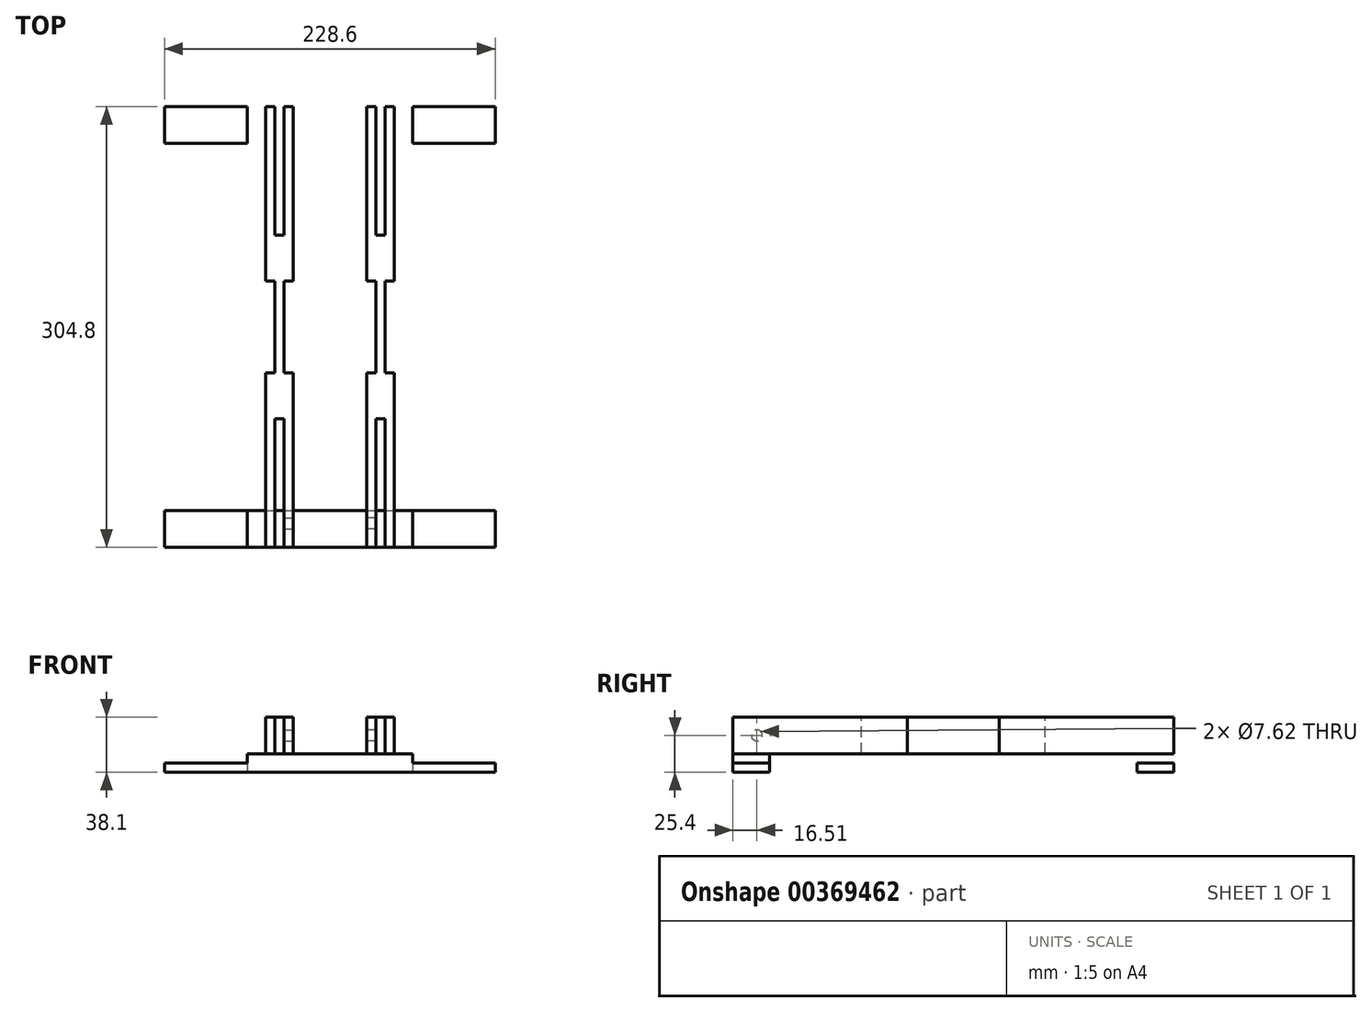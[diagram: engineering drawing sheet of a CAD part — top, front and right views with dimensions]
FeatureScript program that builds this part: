
annotation { "Feature Type Name" : "Feature", "Feature Type Description" : "" }
export const myFeature = defineFeature(function(context is Context, id is Id, definition is map)
    precondition{}
    {
        {
            var Q0;
            Q0=qCreatedBy(makeId("Top.planeOp"),FACE);
            var sketch = newSketch(context, id + "F0", { "sketchPlane" : qUnion([Q0])});
            skLineSegment(sketch, "E0.bottom", {"start": v(-114.3, 152.4) * mm, "end": v(114.3, 152.4) * mm});
            skLineSegment(sketch, "E0.top", {"start": v(-114.3, 127) * mm, "end": v(114.3, 127) * mm});
            skLineSegment(sketch, "E0.left", {"start": v(-114.3, 152.4) * mm, "end": v(-114.3, 127) * mm});
            skLineSegment(sketch, "E0.right", {"start": v(114.3, 152.4) * mm, "end": v(114.3, 127) * mm});
            skLineSegment(sketch, "E1", {"start": v(-113.97, 0) * mm, "end": v(125.77, 0) * mm});
            skLineSegment(sketch, "E2.MirrorCS", {"start": v(-114.3, -152.4) * mm, "end": v(114.3, -152.4) * mm});
            skLineSegment(sketch, "E3.MirrorCS", {"start": v(-114.3, -152.4) * mm, "end": v(-114.3, -127) * mm});
            skLineSegment(sketch, "E4.MirrorCS", {"start": v(-114.3, -127) * mm, "end": v(114.3, -127) * mm});
            skLineSegment(sketch, "E5.MirrorCS", {"start": v(114.3, -152.4) * mm, "end": v(114.3, -127) * mm});
            skLineSegment(sketch, "E6.bottom", {"start": v(-57.15, 152.4) * mm, "end": v(57.15, 152.4) * mm});
            skLineSegment(sketch, "E6.top", {"start": v(-57.15, 127) * mm, "end": v(57.15, 127) * mm});
            skLineSegment(sketch, "E6.left", {"start": v(-57.15, 152.4) * mm, "end": v(-57.15, 127) * mm});
            skLineSegment(sketch, "E6.right", {"start": v(57.15, 152.4) * mm, "end": v(57.15, 127) * mm});
            skLineSegment(sketch, "E7.MirrorCS", {"start": v(-57.15, -127) * mm, "end": v(57.15, -127) * mm});
            skLineSegment(sketch, "E8.MirrorCS", {"start": v(-57.15, -152.4) * mm, "end": v(-57.15, -127) * mm});
            skLineSegment(sketch, "E9.MirrorCS", {"start": v(57.15, -152.4) * mm, "end": v(57.15, -127) * mm});
            skLineSegment(sketch, "E10.MirrorCS", {"start": v(-57.15, -152.4) * mm, "end": v(57.15, -152.4) * mm});
            skLineSegment(sketch, "E11", {"start": v(0, 0) * mm, "end": v(0, -127) * mm});
            skSolve(sketch);
        }
        {
            var Q0;
            {var subQ0=sQuery(id+"F0.wireOp",EDGE,"E5.MirrorCS");Q0=makeQuery(id+"F0.imprint","IMPRINT",FACE,{"disambiguationData":[TD([[makeQuery(id+"F0.imprint","IMPRINT",EDGE,{"derivedFrom":subQ0}),1.0]])]});}
            var Q1;
            {var subQ0=sQuery(id+"F0.wireOp",EDGE,"E3.MirrorCS");Q1=makeQuery(id+"F0.imprint","IMPRINT",FACE,{"disambiguationData":[TD([[makeQuery(id+"F0.imprint","IMPRINT",EDGE,{"derivedFrom":subQ0}),-1.0]])]});}
            var Q2;
            {var subQ0=sQuery(id+"F0.wireOp",EDGE,"E0.left");Q2=makeQuery(id+"F0.imprint","IMPRINT",FACE,{"disambiguationData":[TD([[makeQuery(id+"F0.imprint","IMPRINT",EDGE,{"derivedFrom":subQ0}),1.0]])]});}
            var Q3;
            {var subQ0=sQuery(id+"F0.wireOp",EDGE,"E0.right");Q3=makeQuery(id+"F0.imprint","IMPRINT",FACE,{"disambiguationData":[TD([[makeQuery(id+"F0.imprint","IMPRINT",EDGE,{"derivedFrom":subQ0}),-1.0]])]});}
            extrude(context, id + "F1", {"entities" : qUnion([Q0, Q1, Q2, Q3]), "depth" : 6.35 * mm});
        }
        {
            var Q0;
            Q0=makeQuery(id+"F0.imprint","IMPRINT",FACE,{"disambiguationData":[TD([[makeQuery(id+"F0.imprint","IMPRINT",EDGE,{"derivedFrom":sQuery(id+"F0.wireOp",EDGE,"E8.MirrorCS")}),-1.0]])]});
            var Q1;
            Q1=makeQuery(id+"F0.imprint","IMPRINT",FACE,{"disambiguationData":[TD([[makeQuery(id+"F0.imprint","IMPRINT",EDGE,{"derivedFrom":sQuery(id+"F0.wireOp",EDGE,"E6.bottom")}),-1.0]])]});
            extrude(context, id + "F2", {"entities" : qUnion([Q0, Q1]), "depth" : 12.7 * mm});
        }
        {
            var Q0;
            Q0=makeQuery(id+"F1.opExtrude","SWEPT_BODY",BODY,{"disambiguationData":[OSD([sQuery(id+"F0.wireOp",EDGE,"E0.bottom"),sQuery(id+"F0.wireOp",EDGE,"E0.top"),sQuery(id+"F0.wireOp",EDGE,"E0.left"),sQuery(id+"F0.wireOp",EDGE,"E6.left")])]});
            var Q1;
            Q1=makeQuery(id+"F1.opExtrude","SWEPT_BODY",BODY,{"disambiguationData":[OSD([sQuery(id+"F0.wireOp",EDGE,"E0.bottom"),sQuery(id+"F0.wireOp",EDGE,"E0.top"),sQuery(id+"F0.wireOp",EDGE,"E0.right"),sQuery(id+"F0.wireOp",EDGE,"E6.right")])]});
            var Q2;
            Q2=makeQuery(id+"F1.opExtrude","SWEPT_BODY",BODY,{"disambiguationData":[OSD([sQuery(id+"F0.wireOp",EDGE,"E2.MirrorCS"),sQuery(id+"F0.wireOp",EDGE,"E3.MirrorCS"),sQuery(id+"F0.wireOp",EDGE,"E4.MirrorCS"),sQuery(id+"F0.wireOp",EDGE,"E8.MirrorCS")])]});
            var Q3;
            Q3=makeQuery(id+"F1.opExtrude","SWEPT_BODY",BODY,{"disambiguationData":[OSD([sQuery(id+"F0.wireOp",EDGE,"E2.MirrorCS"),sQuery(id+"F0.wireOp",EDGE,"E4.MirrorCS"),sQuery(id+"F0.wireOp",EDGE,"E5.MirrorCS"),sQuery(id+"F0.wireOp",EDGE,"E9.MirrorCS")])]});
            var Q4;
            Q4=makeQuery(id+"F2.opExtrude","SWEPT_BODY",BODY,{"disambiguationData":[OSD([sQuery(id+"F0.wireOp",EDGE,"E6.bottom"),sQuery(id+"F0.wireOp",EDGE,"E6.top"),sQuery(id+"F0.wireOp",EDGE,"E6.left"),sQuery(id+"F0.wireOp",EDGE,"E6.right")])]});
            var Q5;
            Q5=makeQuery(id+"F2.opExtrude","SWEPT_BODY",BODY,{"disambiguationData":[OSD([sQuery(id+"F0.wireOp",EDGE,"E8.MirrorCS"),sQuery(id+"F0.wireOp",EDGE,"E9.MirrorCS"),sQuery(id+"F0.wireOp",EDGE,"E10.MirrorCS"),sQuery(id+"F0.wireOp",EDGE,"E7.MirrorCS")])]});
            booleanBodies(context, id + "F3", {"operationType" : BooleanOperationType.UNION, "tools" : qUnion([Q0, Q1, Q2, Q3, Q4, Q5])});
        }
        {
            var Q0;
            {var subQ0=sQuery(id+"F0.wireOp",EDGE,"E10.MirrorCS");var subQ1=sQuery(id+"F0.wireOp",EDGE,"E2.MirrorCS");Q0=makeQuery(id+"F3.opBoolean","MERGE",FACE,{"derivedFrom":[makeQuery(id+"F1.opExtrude","SWEPT_FACE",FACE,{"disambiguationData":[OSD([subQ1]),TDD([makeQuery(id+"F0.imprint","IMPRINT",EDGE,{"disambiguationData":[TD([[makeQuery(id+"F0.imprint","INTERSECT",VERTEX,{"derivedFrom":[subQ1,sQuery(id+"F0.wireOp",EDGE,"E3.MirrorCS")]}),-1.0]])],"derivedFrom":subQ1})])]}),makeQuery(id+"F1.opExtrude","SWEPT_FACE",FACE,{"disambiguationData":[OSD([subQ1]),TDD([makeQuery(id+"F0.imprint","IMPRINT",EDGE,{"disambiguationData":[TD([[makeQuery(id+"F0.imprint","INTERSECT",VERTEX,{"derivedFrom":[subQ1,sQuery(id+"F0.wireOp",EDGE,"E5.MirrorCS")]}),1.0]])],"derivedFrom":subQ1})])]}),makeQuery(id+"F2.opExtrude","SWEPT_FACE",FACE,{"disambiguationData":[OSD([subQ0])]})]});}
            var sketch = newSketch(context, id + "F4", { "sketchPlane" : qUnion([Q0])});
            skLineSegment(sketch, "E12", {"start": v(0, 59.29) * mm, "end": v(0, 0) * mm});
            skLineSegment(sketch, "E13.bottom", {"start": v(-44.45, 12.7) * mm, "end": v(-38.1, 12.7) * mm});
            skLineSegment(sketch, "E13.top", {"start": v(-44.45, 38.1) * mm, "end": v(-38.1, 38.1) * mm});
            skLineSegment(sketch, "E13.left", {"start": v(-44.45, 12.7) * mm, "end": v(-44.45, 38.1) * mm});
            skLineSegment(sketch, "E13.right", {"start": v(-38.1, 12.7) * mm, "end": v(-38.1, 38.1) * mm});
            skLineSegment(sketch, "E14.bottom", {"start": v(-31.75, 12.7) * mm, "end": v(-25.4, 12.7) * mm});
            skLineSegment(sketch, "E14.top", {"start": v(-31.75, 38.1) * mm, "end": v(-25.4, 38.1) * mm});
            skLineSegment(sketch, "E14.left", {"start": v(-31.75, 12.7) * mm, "end": v(-31.75, 38.1) * mm});
            skLineSegment(sketch, "E14.right", {"start": v(-25.4, 12.7) * mm, "end": v(-25.4, 38.1) * mm});
            skLineSegment(sketch, "E15.MirrorCS", {"start": v(25.4, 12.7) * mm, "end": v(25.4, 38.1) * mm});
            skLineSegment(sketch, "E16.MirrorCS", {"start": v(31.75, 38.1) * mm, "end": v(25.4, 38.1) * mm});
            skLineSegment(sketch, "E17.MirrorCS", {"start": v(31.75, 12.7) * mm, "end": v(25.4, 12.7) * mm});
            skLineSegment(sketch, "E18.MirrorCS", {"start": v(31.75, 12.7) * mm, "end": v(31.75, 38.1) * mm});
            skLineSegment(sketch, "E19.MirrorCS", {"start": v(38.1, 12.7) * mm, "end": v(38.1, 38.1) * mm});
            skLineSegment(sketch, "E20.MirrorCS", {"start": v(44.45, 12.7) * mm, "end": v(44.45, 38.1) * mm});
            skLineSegment(sketch, "E21.MirrorCS", {"start": v(44.45, 38.1) * mm, "end": v(38.1, 38.1) * mm});
            skLineSegment(sketch, "E22.MirrorCS", {"start": v(44.45, 12.7) * mm, "end": v(38.1, 12.7) * mm});
            skLineSegment(sketch, "E23.bottom", {"start": v(-38.1, 38.1) * mm, "end": v(-31.75, 38.1) * mm});
            skLineSegment(sketch, "E23.top", {"start": v(-38.1, 12.7) * mm, "end": v(-31.75, 12.7) * mm});
            skLineSegment(sketch, "E23.left", {"start": v(-38.1, 38.1) * mm, "end": v(-38.1, 12.7) * mm});
            skLineSegment(sketch, "E23.right", {"start": v(-31.75, 38.1) * mm, "end": v(-31.75, 12.7) * mm});
            skLineSegment(sketch, "E24.bottom", {"start": v(31.75, 38.1) * mm, "end": v(38.1, 38.1) * mm});
            skLineSegment(sketch, "E24.top", {"start": v(31.75, 12.7) * mm, "end": v(38.1, 12.7) * mm});
            skLineSegment(sketch, "E24.left", {"start": v(31.75, 38.1) * mm, "end": v(31.75, 12.7) * mm});
            skLineSegment(sketch, "E24.right", {"start": v(38.1, 38.1) * mm, "end": v(38.1, 12.7) * mm});
            skSolve(sketch);
        }
        {
            var Q0;
            Q0=makeQuery(id+"F4.imprint","IMPRINT",FACE,{"disambiguationData":[TD([[makeQuery(id+"F4.imprint","IMPRINT",EDGE,{"derivedFrom":sQuery(id+"F4.wireOp",EDGE,"E13.bottom")}),1.0]])]});
            var Q1;
            Q1=makeQuery(id+"F4.imprint","IMPRINT",FACE,{"disambiguationData":[TD([[makeQuery(id+"F4.imprint","IMPRINT",EDGE,{"derivedFrom":sQuery(id+"F4.wireOp",EDGE,"E14.bottom")}),1.0]])]});
            var Q2;
            Q2=makeQuery(id+"F4.imprint","IMPRINT",FACE,{"disambiguationData":[TD([[makeQuery(id+"F4.imprint","IMPRINT",EDGE,{"derivedFrom":sQuery(id+"F4.wireOp",EDGE,"E19.MirrorCS")}),-1.0]])]});
            var Q3;
            Q3=makeQuery(id+"F4.imprint","IMPRINT",FACE,{"disambiguationData":[TD([[makeQuery(id+"F4.imprint","IMPRINT",EDGE,{"derivedFrom":sQuery(id+"F4.wireOp",EDGE,"E23.bottom")}),-1.0]])]});
            var Q4;
            Q4=makeQuery(id+"F4.imprint","IMPRINT",FACE,{"disambiguationData":[TD([[makeQuery(id+"F4.imprint","IMPRINT",EDGE,{"derivedFrom":sQuery(id+"F4.wireOp",EDGE,"E15.MirrorCS")}),-1.0]])]});
            var Q5;
            Q5=makeQuery(id+"F4.imprint","IMPRINT",FACE,{"disambiguationData":[TD([[makeQuery(id+"F4.imprint","IMPRINT",EDGE,{"derivedFrom":sQuery(id+"F4.wireOp",EDGE,"E24.bottom")}),-1.0]])]});
            var Q6;
            Q6=makeQuery(id+"F4.imprint","IMPRINT",FACE,{"disambiguationData":[TD([[makeQuery(id+"F4.imprint","IMPRINT",EDGE,{"derivedFrom":sQuery(id+"F4.wireOp",EDGE,"E20.MirrorCS")}),1.0]])]});
            extrude(context, id + "F5", {"entities" : qUnion([Q0, Q1, Q2, Q3, Q4, Q5, Q6]), "oppositeDirection" : true, "depth" : 304.8 * mm});
        }
        {
            var Q0;
            Q0=makeQuery(id+"F5.opExtrude","SWEPT_FACE",FACE,{"disambiguationData":[OSD([sQuery(id+"F4.wireOp",EDGE,"E13.left")])]});
            var sketch = newSketch(context, id + "F6", { "sketchPlane" : qUnion([Q0])});
            skLineSegment(sketch, "E25.bottom", {"start": v(-31.75, 12.7) * mm, "end": v(31.75, 12.7) * mm});
            skLineSegment(sketch, "E25.top", {"start": v(-31.75, 38.1) * mm, "end": v(31.75, 38.1) * mm});
            skLineSegment(sketch, "E25.left", {"start": v(-31.75, 12.7) * mm, "end": v(-31.75, 38.1) * mm});
            skLineSegment(sketch, "E25.right", {"start": v(31.75, 12.7) * mm, "end": v(31.75, 38.1) * mm});
            skSolve(sketch);
        }
        {
            var Q0;
            Q0=makeQuery(id+"F6.imprint","IMPRINT",FACE,{"disambiguationData":[TD([[makeQuery(id+"F6.imprint","IMPRINT",EDGE,{"derivedFrom":sQuery(id+"F6.wireOp",EDGE,"E25.bottom")}),1.0]])]});
            extrude(context, id + "F7", {"entities" : qUnion([Q0]), "operationType" : NewBodyOperationType.REMOVE, "oppositeDirection" : true, "depth" : 6.35 * mm});
        }
        {
            var Q0;
            Q0=makeQuery(id+"F5.opExtrude","SWEPT_FACE",FACE,{"disambiguationData":[OSD([sQuery(id+"F4.wireOp",EDGE,"E14.right")])]});
            var sketch = newSketch(context, id + "F8", { "sketchPlane" : qUnion([Q0])});
            skLineSegment(sketch, "E26.bottom", {"start": v(-31.75, 38.1) * mm, "end": v(31.75, 38.1) * mm});
            skLineSegment(sketch, "E26.top", {"start": v(-31.75, 12.7) * mm, "end": v(31.75, 12.7) * mm});
            skLineSegment(sketch, "E26.left", {"start": v(-31.75, 38.1) * mm, "end": v(-31.75, 12.7) * mm});
            skLineSegment(sketch, "E26.right", {"start": v(31.75, 38.1) * mm, "end": v(31.75, 12.7) * mm});
            skSolve(sketch);
        }
        {
            var Q0;
            Q0=qSketchRegion(id+"F8",true);
            extrude(context, id + "F9", {"entities" : qUnion([Q0]), "operationType" : NewBodyOperationType.REMOVE, "oppositeDirection" : true, "depth" : 6.35 * mm});
        }
        {
            var Q0;
            Q0=makeQuery(id+"F5.opExtrude","SWEPT_FACE",FACE,{"disambiguationData":[OSD([sQuery(id+"F4.wireOp",EDGE,"E20.MirrorCS")])]});
            var sketch = newSketch(context, id + "F10", { "sketchPlane" : qUnion([Q0])});
            skLineSegment(sketch, "E27.bottom", {"start": v(-31.75, 38.1) * mm, "end": v(31.75, 38.1) * mm});
            skLineSegment(sketch, "E27.top", {"start": v(-31.75, 12.7) * mm, "end": v(31.75, 12.7) * mm});
            skLineSegment(sketch, "E27.left", {"start": v(-31.75, 38.1) * mm, "end": v(-31.75, 12.7) * mm});
            skLineSegment(sketch, "E27.right", {"start": v(31.75, 38.1) * mm, "end": v(31.75, 12.7) * mm});
            skSolve(sketch);
        }
        {
            var Q0;
            Q0=makeQuery(id+"F10.imprint","IMPRINT",FACE,{"disambiguationData":[TD([[makeQuery(id+"F10.imprint","IMPRINT",EDGE,{"derivedFrom":sQuery(id+"F10.wireOp",EDGE,"E27.bottom")}),1.0]])]});
            extrude(context, id + "F11", {"entities" : qUnion([Q0]), "operationType" : NewBodyOperationType.REMOVE, "oppositeDirection" : true, "depth" : 6.35 * mm});
        }
        {
            var Q0;
            Q0=makeQuery(id+"F5.opExtrude","SWEPT_FACE",FACE,{"disambiguationData":[OSD([sQuery(id+"F4.wireOp",EDGE,"E15.MirrorCS")])]});
            var sketch = newSketch(context, id + "F12", { "sketchPlane" : qUnion([Q0])});
            skLineSegment(sketch, "E28.bottom", {"start": v(-31.75, 38.1) * mm, "end": v(31.75, 38.1) * mm});
            skLineSegment(sketch, "E28.top", {"start": v(-31.75, 12.7) * mm, "end": v(31.75, 12.7) * mm});
            skLineSegment(sketch, "E28.left", {"start": v(-31.75, 38.1) * mm, "end": v(-31.75, 12.7) * mm});
            skLineSegment(sketch, "E28.right", {"start": v(31.75, 38.1) * mm, "end": v(31.75, 12.7) * mm});
            skSolve(sketch);
        }
        {
            var Q0;
            Q0=qSketchRegion(id+"F12",true);
            extrude(context, id + "F13", {"entities" : qUnion([Q0]), "operationType" : NewBodyOperationType.REMOVE, "oppositeDirection" : true, "depth" : 6.35 * mm});
        }
        {
            var Q0;
            Q0=makeQuery(id+"F5.opExtrude","SWEPT_FACE",FACE,{"disambiguationData":[OSD([sQuery(id+"F4.wireOp",EDGE,"E13.top"),sQuery(id+"F4.wireOp",EDGE,"E14.top"),sQuery(id+"F4.wireOp",EDGE,"E23.bottom")])]});
            var sketch = newSketch(context, id + "F14", { "sketchPlane" : qUnion([Q0])});
            skLineSegment(sketch, "E29", {"start": v(0, 158.09) * mm, "end": v(0, -156.8) * mm});
            skLineSegment(sketch, "E30.bottom", {"start": v(-38.1, 63.5) * mm, "end": v(-31.75, 63.5) * mm});
            skLineSegment(sketch, "E30.top", {"start": v(-38.1, 152.4) * mm, "end": v(-31.75, 152.4) * mm});
            skLineSegment(sketch, "E30.left", {"start": v(-38.1, 63.5) * mm, "end": v(-38.1, 152.4) * mm});
            skLineSegment(sketch, "E30.right", {"start": v(-31.75, 63.5) * mm, "end": v(-31.75, 152.4) * mm});
            skLineSegment(sketch, "E31", {"start": v(-107.54, 0) * mm, "end": v(83.71, 0) * mm});
            skLineSegment(sketch, "E32.MirrorCS", {"start": v(-31.75, -63.5) * mm, "end": v(-31.75, -152.4) * mm});
            skLineSegment(sketch, "E33.MirrorCS", {"start": v(-38.1, -63.5) * mm, "end": v(-38.1, -152.4) * mm});
            skLineSegment(sketch, "E34", {"start": v(-38.1, -63.5) * mm, "end": v(-31.75, -63.5) * mm});
            skLineSegment(sketch, "E35", {"start": v(-31.75, -152.4) * mm, "end": v(-38.1, -152.4) * mm});
            skLineSegment(sketch, "E36.MirrorCS", {"start": v(38.1, 63.5) * mm, "end": v(38.1, 152.4) * mm});
            skLineSegment(sketch, "E37.MirrorCS", {"start": v(31.75, 63.5) * mm, "end": v(31.75, 152.4) * mm});
            skLineSegment(sketch, "E38.MirrorCS", {"start": v(38.1, -63.5) * mm, "end": v(38.1, -152.4) * mm});
            skLineSegment(sketch, "E39.MirrorCS", {"start": v(31.75, -63.5) * mm, "end": v(31.75, -152.4) * mm});
            skLineSegment(sketch, "E40", {"start": v(31.75, 152.4) * mm, "end": v(38.1, 152.4) * mm});
            skLineSegment(sketch, "E41", {"start": v(31.75, 63.5) * mm, "end": v(38.1, 63.5) * mm});
            skLineSegment(sketch, "E42", {"start": v(31.75, -63.5) * mm, "end": v(38.1, -63.5) * mm});
            skLineSegment(sketch, "E43", {"start": v(31.75, -152.4) * mm, "end": v(38.1, -152.4) * mm});
            skSolve(sketch);
        }
        {
            var Q0;
            Q0=qSketchRegion(id+"F14",true);
            extrude(context, id + "F15", {"entities" : qUnion([Q0]), "operationType" : NewBodyOperationType.REMOVE, "oppositeDirection" : true, "depth" : 25.4 * mm});
        }
        {
            var Q0;
            {var subQ2=sQuery(id+"F4.wireOp",EDGE,"E14.right");Q0=makeQuery(id+"F9.boolean.opBoolean","SPLIT",FACE,{"disambiguationData":[TD([makeQuery(id+"F9.opExtrude","SWEPT_FACE",FACE,{"disambiguationData":[OSD([sQuery(id+"F8.wireOp",EDGE,"E26.left")])]})])],"derivedFrom":makeQuery(id+"F5.opExtrude","SWEPT_FACE",FACE,{"disambiguationData":[OSD([subQ2])]})});}
            var sketch = newSketch(context, id + "F16", { "sketchPlane" : qUnion([Q0])});
            skCircle(sketch, "E44", {"center": v(-135.9, 25.4) * mm, "radius": 3.81 * mm});
            skSolve(sketch);
        }
        {
            var Q0;
            Q0=qSketchRegion(id+"F16",true);
            extrude(context, id + "F17", {"entities" : qUnion([Q0]), "operationType" : NewBodyOperationType.REMOVE, "oppositeDirection" : true, "depth" : 6.35 * mm});
        }
        {
            var Q0;
            {var subQ6=sQuery(id+"F4.wireOp",EDGE,"E15.MirrorCS");Q0=makeQuery(id+"F13.boolean.opBoolean","SPLIT",FACE,{"disambiguationData":[TD([makeQuery(id+"F13.opExtrude","SWEPT_FACE",FACE,{"disambiguationData":[OSD([sQuery(id+"F12.wireOp",EDGE,"E28.right")])]})])],"derivedFrom":makeQuery(id+"F5.opExtrude","SWEPT_FACE",FACE,{"disambiguationData":[OSD([subQ6])]})});}
            var sketch = newSketch(context, id + "F18", { "sketchPlane" : qUnion([Q0])});
            skCircle(sketch, "E45", {"center": v(135.89, 25.4) * mm, "radius": 3.81 * mm});
            skSolve(sketch);
        }
        {
            var Q0;
            Q0=qSketchRegion(id+"F18",true);
            extrude(context, id + "F19", {"entities" : qUnion([Q0]), "operationType" : NewBodyOperationType.REMOVE, "oppositeDirection" : true, "depth" : 6.35 * mm});
        }
    });
